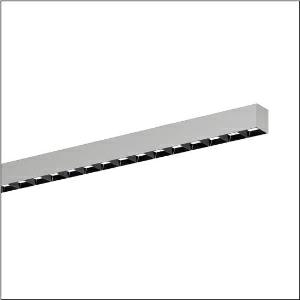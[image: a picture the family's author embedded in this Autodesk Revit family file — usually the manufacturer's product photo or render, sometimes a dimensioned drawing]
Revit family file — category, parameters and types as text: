
# Revit family: silica_r__21_51mx21dc4asb_ccd6
name_source: partatom
category: Lighting Fixtures
units: mm (PartAtom-declared; Revit-internal decimal feet)

## family parameters
Cut with Voids When Loaded = No
Host = Face
Light Source = No
Part Type = Normal
Room Calculation Point = No
Round Connector Dimension = Use Diameter
Shared = No

## types (1)
- --- (1 x LED, 10800 lm, 64.8 W, 4000K)
    Apparent Load = 65 VA
    CIE Flux Codes = 87 99 100 100 100
    Color Rendering = 80
    Color Temperature = 4000K
    Default Elevation = 1800 mm
    Description = Silica® 21, office luminaire, primary light control with darklight reflector, of PMMA, black, CAT 2 (L<= 3000cd/m²), light emission: direct distribution, primary light characteristic: symmetric, installation type: surface-mounted, LED, rated luminous flux: 10.800lm, luminous efficacy: 167lm/W, light colour: 840, colour temperature: 4000K, with terminal, 3+2-pole, max. 2.5mm², mains connection: 220..240V, AC, 50/60Hz, rated input power: 64.8W, luminaire housing, of aluminium, metallic grey (RAL 9006), length: 3.004mm, width: 53mm, height: 53mm, protection rating (complete): IP20, insulation class (complete): insulation class I (protective earthing), certification: CE, permissible operating ambient temperature: 0..+35°C, standard: EN 50419, packaging unit: 1 piece
    Height = 0 mm  [stored 0 ft]
    Lamp = 1 x LED
    Lamp Light Flux = 10800 lm
    Lamp Power = 64.8 W
    Lamp count = 1
    Length = 3004 mm
    Luminous efficacy = 167 lm/W
    Manufacturer = Siteco
    ModVariant = No
    Model = 51MX21DC4ASB
    Mounting Place = Ceiling
    Mounting Type = Recessed
    Number of Poles = 1
    OnlyDefault = Yes
    Power Factor = 1
    Product Name = Silica® 21
    Product group = office luminaire | ceiling recessed
    ProductGroupID = 401
    Protection Class = Protection class I
    Protection Degree = IP 20
    RLX_Detail_Level = 1
    RLX_Emergency_Light_Flux = 0 lm
    RLX_Emergency_Type = 0
    RLX_Emergency_Type_DB = No
    RlxData = <blob elided: 63637 chars, md5=1c211a58>
    Socket = socket
    Standby Power = 0 W
    System Light Flux = 10800 lm
    System Power = 65 W
    Type Comments = factory setting: luminous flux: 100 % | dim-lin: 254 | 367 mA
    Type Image = l_1297764.jpg
    URL = http://relux.com
    VarID = @adj_054317
    Voltage = 0 V
    Weight = 0.00 kg
    Width = 53 mm

note: [stored X ft] marks values corroborated as IEEE doubles in the binary element streams (Revit-internal decimal feet)

## geometry (parser evidence)
native form markers: Blend x4, Sweep x11
no freeform markers — native parametric forms only
